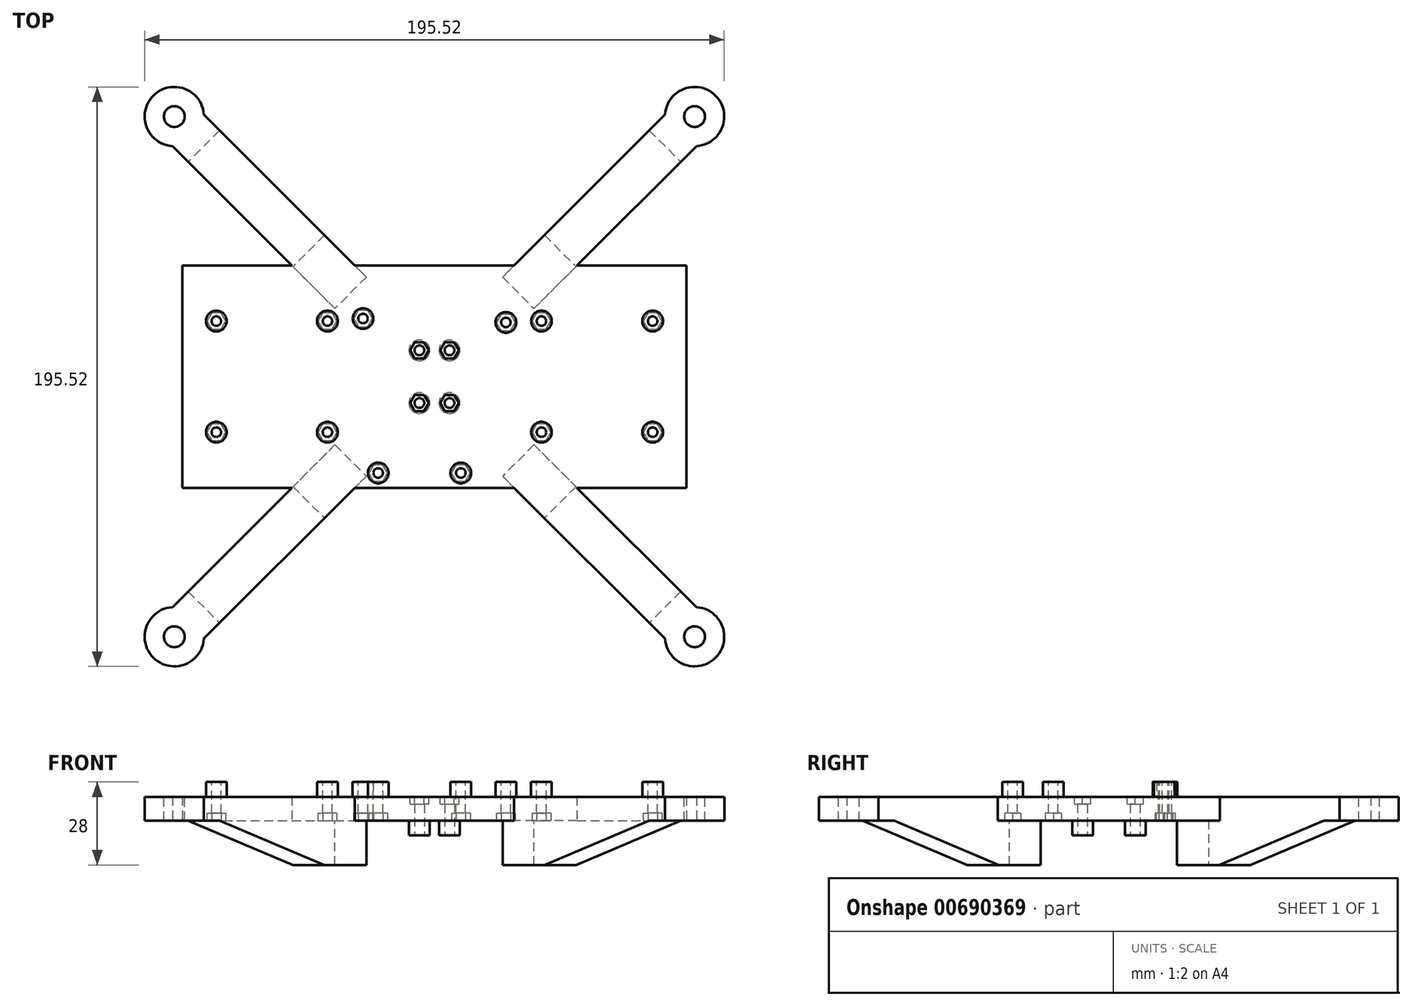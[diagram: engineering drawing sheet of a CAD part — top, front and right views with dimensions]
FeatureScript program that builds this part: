
annotation { "Feature Type Name" : "Feature", "Feature Type Description" : "" }
export const myFeature = defineFeature(function(context is Context, id is Id, definition is map)
    precondition{}
    {
        {
            var Q0;
            Q0=qCreatedBy(makeId("Top.planeOp"),FACE);
            var sketch = newSketch(context, id + "F0", { "sketchPlane" : qUnion([Q0])});
            skLineSegment(sketch, "E0.left", {"start": v(-85, 37.5) * mm, "end": v(-85, -37.5) * mm});
            skLineSegment(sketch, "E0.right", {"start": v(85, 37.5) * mm, "end": v(85, -37.5) * mm});
            skPoint(sketch, "E0.middle", {"position": v(0, 0) * mm});
            skLineSegment(sketch, "E1", {"start": v(-10.6, 0) * mm, "end": v(-48.1, 37.5) * mm, "construction": true});
            skLineSegment(sketch, "E2", {"start": v(-48.1, 37.5) * mm, "end": v(-88.39, 77.78) * mm});
            skLineSegment(sketch, "E3", {"start": v(0, 10.6) * mm, "end": v(-26.9, 37.5) * mm, "construction": true});
            skLineSegment(sketch, "E4", {"start": v(-26.9, 37.5) * mm, "end": v(-77.78, 88.39) * mm});
            skLineSegment(sketch, "E5", {"start": v(0, 10.6) * mm, "end": v(26.9, 37.5) * mm, "construction": true});
            skLineSegment(sketch, "E6", {"start": v(26.9, 37.5) * mm, "end": v(77.78, 88.39) * mm});
            skLineSegment(sketch, "E7", {"start": v(10.6, 0) * mm, "end": v(48.1, 37.5) * mm, "construction": true});
            skLineSegment(sketch, "E8", {"start": v(48.1, 37.5) * mm, "end": v(88.39, 77.78) * mm});
            skLineSegment(sketch, "E9", {"start": v(-10.6, 0) * mm, "end": v(-48.1, -37.5) * mm, "construction": true});
            skLineSegment(sketch, "E10", {"start": v(-48.1, -37.5) * mm, "end": v(-88.39, -77.78) * mm});
            skLineSegment(sketch, "E11", {"start": v(0, -10.6) * mm, "end": v(-26.9, -37.5) * mm, "construction": true});
            skLineSegment(sketch, "E12", {"start": v(-26.9, -37.5) * mm, "end": v(-77.78, -88.39) * mm});
            skLineSegment(sketch, "E13", {"start": v(0, -10.6) * mm, "end": v(26.9, -37.5) * mm, "construction": true});
            skLineSegment(sketch, "E14", {"start": v(26.9, -37.5) * mm, "end": v(77.78, -88.39) * mm});
            skLineSegment(sketch, "E15", {"start": v(10.6, 0) * mm, "end": v(48.1, -37.5) * mm, "construction": true});
            skLineSegment(sketch, "E16", {"start": v(48.1, -37.5) * mm, "end": v(88.39, -77.78) * mm});
            skLineSegment(sketch, "E17", {"start": v(0, 10.6) * mm, "end": v(0, -10.6) * mm, "construction": true});
            skLineSegment(sketch, "E18", {"start": v(-10.6, 0) * mm, "end": v(10.6, 0) * mm, "construction": true});
            skLineSegment(sketch, "E19", {"start": v(-85, 37.5) * mm, "end": v(-48.1, 37.5) * mm});
            skLineSegment(sketch, "E20", {"start": v(-26.9, 37.5) * mm, "end": v(26.9, 37.5) * mm});
            skLineSegment(sketch, "E21", {"start": v(85, 37.5) * mm, "end": v(48.1, 37.5) * mm});
            skLineSegment(sketch, "E22", {"start": v(-85, -37.5) * mm, "end": v(-48.1, -37.5) * mm});
            skLineSegment(sketch, "E23", {"start": v(-26.9, -37.5) * mm, "end": v(26.9, -37.5) * mm});
            skLineSegment(sketch, "E24", {"start": v(48.1, -37.5) * mm, "end": v(85, -37.5) * mm});
            skArc(sketch, "E25", {"start": v(-77.78, 88.39) * mm, "mid": v(-94.83, 94.83) * mm, "end": v(-88.39, 77.78) * mm});
            skArc(sketch, "E26", {"start": v(77.78, 88.39) * mm, "mid": v(94.83, 94.83) * mm, "end": v(88.39, 77.78) * mm});
            skArc(sketch, "E27", {"start": v(88.39, -77.78) * mm, "mid": v(94.83, -94.83) * mm, "end": v(77.78, -88.39) * mm});
            skArc(sketch, "E28", {"start": v(-88.39, -77.78) * mm, "mid": v(-94.83, -94.83) * mm, "end": v(-77.78, -88.39) * mm});
            skSolve(sketch);
        }
        {
            var Q0;
            Q0 = qSketchRegion(id + "F0", true);
            extrude(context, id + "F1", {"entities" : qUnion([Q0]), "endBound" : BoundingType.SYMMETRIC, "depth" : 8 * mm, "offsetDistance" : 25.4 * mm});
        }
        {
            var Q0;
            Q0=makeQuery(id+"F1.opExtrude","SWEPT_FACE",FACE,{"disambiguationData":[OSD([sQuery(id+"F0.wireOp",EDGE,"E12")])]});
            cPlane(context, id + "F2", {"entities" : qUnion([Q0]), "cplaneType" : CPlaneType.OFFSET, "offset" : 0 * mm, "width" : 152.4 * mm, "height" : 152.4 * mm});
        }
        {
            var Q0;
            Q0=qCreatedBy(id+"F2.planeOp",FACE);
            var sketch = newSketch(context, id + "F3", { "sketchPlane" : qUnion([Q0])});
            skLineSegment(sketch, "E29", {"start": v(-110, -4) * mm, "end": v(-60, -19) * mm});
            skLineSegment(sketch, "E30", {"start": v(-60, -19) * mm, "end": v(-40, -19) * mm});
            skLineSegment(sketch, "E31", {"start": v(-40, -19) * mm, "end": v(-40, -4) * mm});
            skLineSegment(sketch, "E32", {"start": v(-40, -4) * mm, "end": v(-110, -4) * mm});
            skLineSegment(sketch, "E33", {"start": v(0, 36.74) * mm, "end": v(0, -57.68) * mm, "construction": true});
            skLineSegment(sketch, "E34.MirrorCS", {"start": v(40, -19) * mm, "end": v(40, -4) * mm});
            skLineSegment(sketch, "E35.MirrorCS", {"start": v(40, -4) * mm, "end": v(110, -4) * mm});
            skLineSegment(sketch, "E36.MirrorCS", {"start": v(110, -4) * mm, "end": v(60, -19) * mm});
            skLineSegment(sketch, "E37.MirrorCS", {"start": v(60, -19) * mm, "end": v(40, -19) * mm});
            skSolve(sketch);
        }
        {
            var Q0;
            Q0 = qSketchRegion(id + "F3", true);
            var Q1;
            Q1=makeQuery(id+"F1.opExtrude","SWEPT_FACE",FACE,{"disambiguationData":[OSD([sQuery(id+"F0.wireOp",EDGE,"E10")])]});
            extrude(context, id + "F4", {"entities" : qUnion([Q0]), "operationType" : NewBodyOperationType.ADD, "endBound" : BoundingType.UP_TO_SURFACE, "oppositeDirection" : true, "depth" : 15 * mm, "endBoundEntityFace" : qUnion([Q1]), "offsetDistance" : 25.4 * mm});
        }
        {
            var Q0;
            Q0=makeQuery(id+"F1.opExtrude","SWEPT_FACE",FACE,{"disambiguationData":[OSD([sQuery(id+"F0.wireOp",EDGE,"E2")])]});
            cPlane(context, id + "F5", {"entities" : qUnion([Q0]), "cplaneType" : CPlaneType.OFFSET, "offset" : 0 * mm, "width" : 152.4 * mm, "height" : 152.4 * mm});
        }
        {
            var Q0;
            Q0=qCreatedBy(id+"F5.planeOp",FACE);
            var sketch = newSketch(context, id + "F6", { "sketchPlane" : qUnion([Q0])});
            skLineSegment(sketch, "E38", {"start": v(0, 30.92) * mm, "end": v(0, -51.6) * mm, "construction": true});
            skLineSegment(sketch, "E39", {"start": v(-40, -4) * mm, "end": v(-110, -4) * mm});
            skLineSegment(sketch, "E40", {"start": v(-110, -4) * mm, "end": v(-60, -19) * mm});
            skLineSegment(sketch, "E41", {"start": v(-60, -19) * mm, "end": v(-40, -19) * mm});
            skLineSegment(sketch, "E42", {"start": v(-40, -19) * mm, "end": v(-40, -4) * mm});
            skLineSegment(sketch, "E43.MirrorCS", {"start": v(40, -19) * mm, "end": v(40, -4) * mm});
            skLineSegment(sketch, "E44.MirrorCS", {"start": v(40, -4) * mm, "end": v(110, -4) * mm});
            skLineSegment(sketch, "E45.MirrorCS", {"start": v(110, -4) * mm, "end": v(60, -19) * mm});
            skLineSegment(sketch, "E46.MirrorCS", {"start": v(60, -19) * mm, "end": v(40, -19) * mm});
            skSolve(sketch);
        }
        {
            var Q0;
            Q0 = qSketchRegion(id + "F6", true);
            var Q1;
            Q1=makeQuery(id+"F1.opExtrude","SWEPT_FACE",FACE,{"disambiguationData":[OSD([sQuery(id+"F0.wireOp",EDGE,"E4")])]});
            extrude(context, id + "F7", {"entities" : qUnion([Q0]), "operationType" : NewBodyOperationType.ADD, "endBound" : BoundingType.UP_TO_SURFACE, "oppositeDirection" : true, "depth" : 25.4 * mm, "endBoundEntityFace" : qUnion([Q1]), "offsetDistance" : 25.4 * mm});
        }
        {
            var Q0;
            Q0=makeQuery(id+"F1.opExtrude","CAP_FACE",FACE,{"disambiguationData":[OSD([sQuery(id+"F0.wireOp",EDGE,"E0.left"),sQuery(id+"F0.wireOp",EDGE,"E0.right"),sQuery(id+"F0.wireOp",EDGE,"E2"),sQuery(id+"F0.wireOp",EDGE,"E4"),sQuery(id+"F0.wireOp",EDGE,"E6"),sQuery(id+"F0.wireOp",EDGE,"E8"),sQuery(id+"F0.wireOp",EDGE,"E10"),sQuery(id+"F0.wireOp",EDGE,"E12"),sQuery(id+"F0.wireOp",EDGE,"E14"),sQuery(id+"F0.wireOp",EDGE,"E16"),sQuery(id+"F0.wireOp",EDGE,"E19"),sQuery(id+"F0.wireOp",EDGE,"E20"),sQuery(id+"F0.wireOp",EDGE,"E21"),sQuery(id+"F0.wireOp",EDGE,"E22"),sQuery(id+"F0.wireOp",EDGE,"E23"),sQuery(id+"F0.wireOp",EDGE,"E24"),sQuery(id+"F0.wireOp",EDGE,"E25"),sQuery(id+"F0.wireOp",EDGE,"E26"),sQuery(id+"F0.wireOp",EDGE,"E27"),sQuery(id+"F0.wireOp",EDGE,"E28")])],"isStart":false});
            var sketch = newSketch(context, id + "F8", { "sketchPlane" : qUnion([Q0])});
            skCircle(sketch, "E47", {"center": v(-87.76, 87.76) * mm, "radius": 3.5 * mm});
            skCircle(sketch, "E48", {"center": v(87.76, 87.76) * mm, "radius": 3.5 * mm});
            skCircle(sketch, "E49", {"center": v(87.76, -87.76) * mm, "radius": 3.5 * mm});
            skCircle(sketch, "E50", {"center": v(-87.76, -87.76) * mm, "radius": 3.5 * mm});
            skSolve(sketch);
        }
        {
            var Q0;
            Q0 = qSketchRegion(id + "F8", true);
            extrude(context, id + "F9", {"entities" : qUnion([Q0]), "operationType" : NewBodyOperationType.REMOVE, "endBound" : BoundingType.THROUGH_ALL, "oppositeDirection" : true, "depth" : 25.4 * mm, "offsetDistance" : 25.4 * mm});
        }
        {
            var Q0;
            Q0=makeQuery(id+"F1.opExtrude","CAP_FACE",FACE,{"disambiguationData":[OSD([sQuery(id+"F0.wireOp",EDGE,"E0.left"),sQuery(id+"F0.wireOp",EDGE,"E0.right"),sQuery(id+"F0.wireOp",EDGE,"E2"),sQuery(id+"F0.wireOp",EDGE,"E4"),sQuery(id+"F0.wireOp",EDGE,"E6"),sQuery(id+"F0.wireOp",EDGE,"E8"),sQuery(id+"F0.wireOp",EDGE,"E10"),sQuery(id+"F0.wireOp",EDGE,"E12"),sQuery(id+"F0.wireOp",EDGE,"E14"),sQuery(id+"F0.wireOp",EDGE,"E16"),sQuery(id+"F0.wireOp",EDGE,"E19"),sQuery(id+"F0.wireOp",EDGE,"E20"),sQuery(id+"F0.wireOp",EDGE,"E21"),sQuery(id+"F0.wireOp",EDGE,"E22"),sQuery(id+"F0.wireOp",EDGE,"E23"),sQuery(id+"F0.wireOp",EDGE,"E24"),sQuery(id+"F0.wireOp",EDGE,"E25"),sQuery(id+"F0.wireOp",EDGE,"E26"),sQuery(id+"F0.wireOp",EDGE,"E27"),sQuery(id+"F0.wireOp",EDGE,"E28")])],"isStart":false});
            var sketch = newSketch(context, id + "F10", { "sketchPlane" : qUnion([Q0])});
            skCircle(sketch, "E51", {"center": v(-24.1, 19.6) * mm, "radius": 1.6 * mm});
            skCircle(sketch, "E52", {"center": v(24.1, 18.3) * mm, "radius": 1.6 * mm});
            skCircle(sketch, "E53", {"center": v(-19, -32.5) * mm, "radius": 1.6 * mm});
            skCircle(sketch, "E54", {"center": v(8.9, -32.5) * mm, "radius": 1.6 * mm});
            skLineSegment(sketch, "E55", {"start": v(-24.1, 19.6) * mm, "end": v(-24.1, 28.34) * mm, "construction": true});
            skLineSegment(sketch, "E56", {"start": v(-24.1, 28.34) * mm, "end": v(24.1, 28.34) * mm, "construction": true});
            skLineSegment(sketch, "E57", {"start": v(24.1, 28.34) * mm, "end": v(24.1, 18.3) * mm, "construction": true});
            skLineSegment(sketch, "E58", {"start": v(0, -37.5) * mm, "end": v(0, 37.5) * mm, "construction": true});
            skLineSegment(sketch, "E59", {"start": v(-19, -32.5) * mm, "end": v(-19, 32.5) * mm, "construction": true});
            skLineSegment(sketch, "E60", {"start": v(-85, 0) * mm, "end": v(85, 0) * mm, "construction": true});
            skCircle(sketch, "E61", {"center": v(-36.1, 18.75) * mm, "radius": 1.6 * mm});
            skCircle(sketch, "E62", {"center": v(-73.6, 18.75) * mm, "radius": 1.6 * mm});
            skCircle(sketch, "E63", {"center": v(-73.6, -18.75) * mm, "radius": 1.6 * mm});
            skCircle(sketch, "E64", {"center": v(-36.1, -18.75) * mm, "radius": 1.6 * mm});
            skLineSegment(sketch, "E65", {"start": v(-73.6, 18.75) * mm, "end": v(-36.1, 18.75) * mm, "construction": true});
            skLineSegment(sketch, "E66", {"start": v(-36.1, -18.75) * mm, "end": v(-36.1, 18.75) * mm, "construction": true});
            skLineSegment(sketch, "E67", {"start": v(-73.6, 18.75) * mm, "end": v(-73.6, -18.75) * mm, "construction": true});
            skLineSegment(sketch, "E68", {"start": v(-73.6, -18.75) * mm, "end": v(-36.1, -18.75) * mm, "construction": true});
            skCircle(sketch, "E69.MirrorC", {"center": v(36.1, 18.75) * mm, "radius": 1.6 * mm});
            skCircle(sketch, "E70.MirrorC", {"center": v(36.1, -18.75) * mm, "radius": 1.6 * mm});
            skCircle(sketch, "E71.MirrorC", {"center": v(73.6, -18.75) * mm, "radius": 1.6 * mm});
            skCircle(sketch, "E72.MirrorC", {"center": v(73.6, 18.75) * mm, "radius": 1.6 * mm});
            skSolve(sketch);
        }
        {
            var Q0;
            Q0 = qSketchRegion(id + "F10", true);
            extrude(context, id + "F11", {"entities" : qUnion([Q0]), "operationType" : NewBodyOperationType.REMOVE, "endBound" : BoundingType.THROUGH_ALL, "oppositeDirection" : true, "depth" : 25.4 * mm, "offsetDistance" : 25.4 * mm});
        }
        {
            var Q0;
            {var subQ0=sQuery(id+"F0.wireOp",EDGE,"E10");var subQ2=sQuery(id+"F0.wireOp",EDGE,"E24");var subQ6=sQuery(id+"F0.wireOp",EDGE,"E19");var subQ9=sQuery(id+"F0.wireOp",EDGE,"E16");var subQ13=sQuery(id+"F0.wireOp",EDGE,"E12");var subQ15=sQuery(id+"F0.wireOp",EDGE,"E23");var subQ18=sQuery(id+"F0.wireOp",EDGE,"E22");var subQ21=sQuery(id+"F0.wireOp",EDGE,"E8");var subQ23=sQuery(id+"F0.wireOp",EDGE,"E21");var subQ25=sQuery(id+"F0.wireOp",EDGE,"E20");var subQ27=sQuery(id+"F0.wireOp",EDGE,"E2");var subQ29=sQuery(id+"F0.wireOp",EDGE,"E0.right");var subQ31=sQuery(id+"F0.wireOp",EDGE,"E4");var subQ33=sQuery(id+"F0.wireOp",EDGE,"E0.left");var subQ34=makeQuery(id+"F1.opExtrude","SWEPT_FACE",FACE,{"disambiguationData":[OSD([subQ33])]});var subQ35=sQuery(id+"F0.wireOp",EDGE,"E6");var subQ38=sQuery(id+"F0.wireOp",EDGE,"E14");var subQ42=sQuery(id+"F0.wireOp",EDGE,"E27");var subQ43=sQuery(id+"F0.wireOp",EDGE,"E25");Q0=makeQuery(id+"F7.boolean.opBoolean","SPLIT",FACE,{"disambiguationData":[TD([subQ34])],"derivedFrom":makeQuery(id+"F4.boolean.opBoolean","SPLIT",FACE,{"disambiguationData":[TD([subQ34])],"derivedFrom":makeQuery(id+"F1.opExtrude","CAP_FACE",FACE,{"disambiguationData":[OSD([subQ33,subQ29,subQ27,subQ31,subQ35,subQ21,subQ0,subQ13,subQ38,subQ9,subQ6,subQ25,subQ23,subQ18,subQ15,subQ2,subQ43,sQuery(id+"F0.wireOp",EDGE,"E26"),subQ42,sQuery(id+"F0.wireOp",EDGE,"E28")])],"isStart":true})})});}
            var sketch = newSketch(context, id + "F12", { "sketchPlane" : qUnion([Q0])});
            skCircle(sketch, "E73.cCircle", {"center": v(-19, 32.5) * mm, "radius": 2.75 * mm, "construction": true});
            skLineSegment(sketch, "E73.0", {"start": v(-22.18, 32.5) * mm, "end": v(-20.59, 35.25) * mm});
            skLineSegment(sketch, "E73.1", {"start": v(-20.59, 35.25) * mm, "end": v(-17.41, 35.25) * mm});
            skLineSegment(sketch, "E73.2", {"start": v(-17.41, 35.25) * mm, "end": v(-15.82, 32.5) * mm});
            skLineSegment(sketch, "E73.3", {"start": v(-15.82, 32.5) * mm, "end": v(-17.41, 29.75) * mm});
            skLineSegment(sketch, "E73.4", {"start": v(-17.41, 29.75) * mm, "end": v(-20.59, 29.75) * mm});
            skLineSegment(sketch, "E73.5", {"start": v(-20.59, 29.75) * mm, "end": v(-22.18, 32.5) * mm});
            skPoint(sketch, "E73.0.midPoint", {"position": v(-21.38, 33.87) * mm});
            skCircle(sketch, "E74.cCircle", {"center": v(8.9, 32.5) * mm, "radius": 2.75 * mm, "construction": true});
            skLineSegment(sketch, "E74.0", {"start": v(5.72, 32.5) * mm, "end": v(7.31, 35.25) * mm});
            skLineSegment(sketch, "E74.1", {"start": v(7.31, 35.25) * mm, "end": v(10.49, 35.25) * mm});
            skLineSegment(sketch, "E74.2", {"start": v(10.49, 35.25) * mm, "end": v(12.08, 32.5) * mm});
            skLineSegment(sketch, "E74.3", {"start": v(12.08, 32.5) * mm, "end": v(10.49, 29.75) * mm});
            skLineSegment(sketch, "E74.4", {"start": v(10.49, 29.75) * mm, "end": v(7.31, 29.75) * mm});
            skLineSegment(sketch, "E74.5", {"start": v(7.31, 29.75) * mm, "end": v(5.72, 32.5) * mm});
            skPoint(sketch, "E74.0.midPoint", {"position": v(6.52, 33.88) * mm});
            skCircle(sketch, "E75.cCircle", {"center": v(36.1, 18.75) * mm, "radius": 2.75 * mm, "construction": true});
            skLineSegment(sketch, "E75.0", {"start": v(32.92, 18.75) * mm, "end": v(34.51, 21.5) * mm});
            skLineSegment(sketch, "E75.1", {"start": v(34.51, 21.5) * mm, "end": v(37.69, 21.5) * mm});
            skLineSegment(sketch, "E75.2", {"start": v(37.69, 21.5) * mm, "end": v(39.28, 18.75) * mm});
            skLineSegment(sketch, "E75.3", {"start": v(39.28, 18.75) * mm, "end": v(37.69, 16) * mm});
            skLineSegment(sketch, "E75.4", {"start": v(37.69, 16) * mm, "end": v(34.51, 16) * mm});
            skLineSegment(sketch, "E75.5", {"start": v(34.51, 16) * mm, "end": v(32.92, 18.75) * mm});
            skPoint(sketch, "E75.0.midPoint", {"position": v(33.72, 20.12) * mm});
            skCircle(sketch, "E76.cCircle", {"center": v(73.6, 18.75) * mm, "radius": 2.75 * mm, "construction": true});
            skLineSegment(sketch, "E76.0", {"start": v(70.42, 18.75) * mm, "end": v(72.01, 21.5) * mm});
            skLineSegment(sketch, "E76.1", {"start": v(72.01, 21.5) * mm, "end": v(75.19, 21.5) * mm});
            skLineSegment(sketch, "E76.2", {"start": v(75.19, 21.5) * mm, "end": v(76.78, 18.75) * mm});
            skLineSegment(sketch, "E76.3", {"start": v(76.78, 18.75) * mm, "end": v(75.19, 16) * mm});
            skLineSegment(sketch, "E76.4", {"start": v(75.19, 16) * mm, "end": v(72.01, 16) * mm});
            skLineSegment(sketch, "E76.5", {"start": v(72.01, 16) * mm, "end": v(70.42, 18.75) * mm});
            skPoint(sketch, "E76.0.midPoint", {"position": v(71.22, 20.12) * mm});
            skCircle(sketch, "E77.cCircle", {"center": v(73.6, -18.75) * mm, "radius": 2.75 * mm, "construction": true});
            skLineSegment(sketch, "E77.0", {"start": v(70.42, -18.75) * mm, "end": v(72.01, -16) * mm});
            skLineSegment(sketch, "E77.1", {"start": v(72.01, -16) * mm, "end": v(75.19, -16) * mm});
            skLineSegment(sketch, "E77.2", {"start": v(75.19, -16) * mm, "end": v(76.78, -18.75) * mm});
            skLineSegment(sketch, "E77.3", {"start": v(76.78, -18.75) * mm, "end": v(75.19, -21.5) * mm});
            skLineSegment(sketch, "E77.4", {"start": v(75.19, -21.5) * mm, "end": v(72.01, -21.5) * mm});
            skLineSegment(sketch, "E77.5", {"start": v(72.01, -21.5) * mm, "end": v(70.42, -18.75) * mm});
            skPoint(sketch, "E77.0.midPoint", {"position": v(71.22, -17.37) * mm});
            skCircle(sketch, "E78.cCircle", {"center": v(36.1, -18.75) * mm, "radius": 2.75 * mm, "construction": true});
            skLineSegment(sketch, "E78.0", {"start": v(34.51, -16) * mm, "end": v(37.69, -16) * mm});
            skLineSegment(sketch, "E78.1", {"start": v(37.69, -16) * mm, "end": v(39.28, -18.75) * mm});
            skLineSegment(sketch, "E78.2", {"start": v(39.28, -18.75) * mm, "end": v(37.69, -21.5) * mm});
            skLineSegment(sketch, "E78.3", {"start": v(37.69, -21.5) * mm, "end": v(34.51, -21.5) * mm});
            skLineSegment(sketch, "E78.4", {"start": v(34.51, -21.5) * mm, "end": v(32.92, -18.75) * mm});
            skLineSegment(sketch, "E78.5", {"start": v(32.92, -18.75) * mm, "end": v(34.51, -16) * mm});
            skPoint(sketch, "E78.0.midPoint", {"position": v(36.1, -16) * mm});
            skCircle(sketch, "E79.cCircle", {"center": v(24.1, -18.3) * mm, "radius": 2.75 * mm, "construction": true});
            skLineSegment(sketch, "E79.0", {"start": v(20.92, -18.3) * mm, "end": v(22.51, -15.55) * mm});
            skLineSegment(sketch, "E79.1", {"start": v(22.51, -15.55) * mm, "end": v(25.69, -15.55) * mm});
            skLineSegment(sketch, "E79.2", {"start": v(25.69, -15.55) * mm, "end": v(27.28, -18.3) * mm});
            skLineSegment(sketch, "E79.3", {"start": v(27.28, -18.3) * mm, "end": v(25.69, -21.05) * mm});
            skLineSegment(sketch, "E79.4", {"start": v(25.69, -21.05) * mm, "end": v(22.51, -21.05) * mm});
            skLineSegment(sketch, "E79.5", {"start": v(22.51, -21.05) * mm, "end": v(20.92, -18.3) * mm});
            skPoint(sketch, "E79.0.midPoint", {"position": v(21.72, -16.93) * mm});
            skCircle(sketch, "E80.cCircle", {"center": v(-24.1, -19.6) * mm, "radius": 2.75 * mm, "construction": true});
            skLineSegment(sketch, "E80.0", {"start": v(-25.69, -16.85) * mm, "end": v(-22.51, -16.85) * mm});
            skLineSegment(sketch, "E80.1", {"start": v(-22.51, -16.85) * mm, "end": v(-20.92, -19.6) * mm});
            skLineSegment(sketch, "E80.2", {"start": v(-20.92, -19.6) * mm, "end": v(-22.51, -22.35) * mm});
            skLineSegment(sketch, "E80.3", {"start": v(-22.51, -22.35) * mm, "end": v(-25.69, -22.35) * mm});
            skLineSegment(sketch, "E80.4", {"start": v(-25.69, -22.35) * mm, "end": v(-27.28, -19.6) * mm});
            skLineSegment(sketch, "E80.5", {"start": v(-27.28, -19.6) * mm, "end": v(-25.69, -16.85) * mm});
            skPoint(sketch, "E80.0.midPoint", {"position": v(-24.1, -16.85) * mm});
            skCircle(sketch, "E81.cCircle", {"center": v(-36.1, -18.75) * mm, "radius": 2.75 * mm, "construction": true});
            skLineSegment(sketch, "E81.0", {"start": v(-37.69, -16) * mm, "end": v(-34.51, -16) * mm});
            skLineSegment(sketch, "E81.1", {"start": v(-34.51, -16) * mm, "end": v(-32.92, -18.75) * mm});
            skLineSegment(sketch, "E81.2", {"start": v(-32.92, -18.75) * mm, "end": v(-34.51, -21.5) * mm});
            skLineSegment(sketch, "E81.3", {"start": v(-34.51, -21.5) * mm, "end": v(-37.69, -21.5) * mm});
            skLineSegment(sketch, "E81.4", {"start": v(-37.69, -21.5) * mm, "end": v(-39.28, -18.75) * mm});
            skLineSegment(sketch, "E81.5", {"start": v(-39.28, -18.75) * mm, "end": v(-37.69, -16) * mm});
            skPoint(sketch, "E81.0.midPoint", {"position": v(-36.1, -16) * mm});
            skCircle(sketch, "E82.cCircle", {"center": v(-36.1, 18.75) * mm, "radius": 2.75 * mm, "construction": true});
            skLineSegment(sketch, "E82.0", {"start": v(-39.28, 18.75) * mm, "end": v(-37.69, 21.5) * mm});
            skLineSegment(sketch, "E82.1", {"start": v(-37.69, 21.5) * mm, "end": v(-34.51, 21.5) * mm});
            skLineSegment(sketch, "E82.2", {"start": v(-34.51, 21.5) * mm, "end": v(-32.92, 18.75) * mm});
            skLineSegment(sketch, "E82.3", {"start": v(-32.92, 18.75) * mm, "end": v(-34.51, 16) * mm});
            skLineSegment(sketch, "E82.4", {"start": v(-34.51, 16) * mm, "end": v(-37.69, 16) * mm});
            skLineSegment(sketch, "E82.5", {"start": v(-37.69, 16) * mm, "end": v(-39.28, 18.75) * mm});
            skPoint(sketch, "E82.0.midPoint", {"position": v(-38.48, 20.12) * mm});
            skCircle(sketch, "E83.cCircle", {"center": v(-73.6, 18.75) * mm, "radius": 2.75 * mm, "construction": true});
            skLineSegment(sketch, "E83.0", {"start": v(-72.01, 21.5) * mm, "end": v(-70.42, 18.75) * mm});
            skLineSegment(sketch, "E83.1", {"start": v(-70.42, 18.75) * mm, "end": v(-72.01, 16) * mm});
            skLineSegment(sketch, "E83.2", {"start": v(-72.01, 16) * mm, "end": v(-75.19, 16) * mm});
            skLineSegment(sketch, "E83.3", {"start": v(-75.19, 16) * mm, "end": v(-76.78, 18.75) * mm});
            skLineSegment(sketch, "E83.4", {"start": v(-76.78, 18.75) * mm, "end": v(-75.19, 21.5) * mm});
            skLineSegment(sketch, "E83.5", {"start": v(-75.19, 21.5) * mm, "end": v(-72.01, 21.5) * mm});
            skPoint(sketch, "E83.0.midPoint", {"position": v(-71.22, 20.12) * mm});
            skCircle(sketch, "E84.cCircle", {"center": v(-73.6, -18.75) * mm, "radius": 2.75 * mm, "construction": true});
            skLineSegment(sketch, "E84.0", {"start": v(-72.01, -16) * mm, "end": v(-70.42, -18.75) * mm});
            skLineSegment(sketch, "E84.1", {"start": v(-70.42, -18.75) * mm, "end": v(-72.01, -21.5) * mm});
            skLineSegment(sketch, "E84.2", {"start": v(-72.01, -21.5) * mm, "end": v(-75.19, -21.5) * mm});
            skLineSegment(sketch, "E84.3", {"start": v(-75.19, -21.5) * mm, "end": v(-76.78, -18.75) * mm});
            skLineSegment(sketch, "E84.4", {"start": v(-76.78, -18.75) * mm, "end": v(-75.19, -16) * mm});
            skLineSegment(sketch, "E84.5", {"start": v(-75.19, -16) * mm, "end": v(-72.01, -16) * mm});
            skPoint(sketch, "E84.0.midPoint", {"position": v(-71.22, -17.37) * mm});
            skSolve(sketch);
        }
        {
            var Q0;
            Q0 = qSketchRegion(id + "F12", true);
            extrude(context, id + "F13", {"entities" : qUnion([Q0]), "operationType" : NewBodyOperationType.REMOVE, "oppositeDirection" : true, "depth" : 2.5 * mm, "offsetDistance" : 25.4 * mm});
        }
        {
            var Q0;
            Q0=makeQuery(id+"F1.opExtrude","CAP_FACE",FACE,{"disambiguationData":[OSD([sQuery(id+"F0.wireOp",EDGE,"E0.left"),sQuery(id+"F0.wireOp",EDGE,"E0.right"),sQuery(id+"F0.wireOp",EDGE,"E2"),sQuery(id+"F0.wireOp",EDGE,"E4"),sQuery(id+"F0.wireOp",EDGE,"E6"),sQuery(id+"F0.wireOp",EDGE,"E8"),sQuery(id+"F0.wireOp",EDGE,"E10"),sQuery(id+"F0.wireOp",EDGE,"E12"),sQuery(id+"F0.wireOp",EDGE,"E14"),sQuery(id+"F0.wireOp",EDGE,"E16"),sQuery(id+"F0.wireOp",EDGE,"E19"),sQuery(id+"F0.wireOp",EDGE,"E20"),sQuery(id+"F0.wireOp",EDGE,"E21"),sQuery(id+"F0.wireOp",EDGE,"E22"),sQuery(id+"F0.wireOp",EDGE,"E23"),sQuery(id+"F0.wireOp",EDGE,"E24"),sQuery(id+"F0.wireOp",EDGE,"E25"),sQuery(id+"F0.wireOp",EDGE,"E26"),sQuery(id+"F0.wireOp",EDGE,"E27"),sQuery(id+"F0.wireOp",EDGE,"E28")])],"isStart":false});
            var sketch = newSketch(context, id + "F14", { "sketchPlane" : qUnion([Q0])});
            skCircle(sketch, "E85", {"center": v(-24.1, 19.6) * mm, "radius": 1.6 * mm});
            skCircle(sketch, "E86", {"center": v(-19, -32.5) * mm, "radius": 1.6 * mm});
            skCircle(sketch, "E87", {"center": v(-19, -32.5) * mm, "radius": 3.5 * mm});
            skCircle(sketch, "E88", {"center": v(-24.1, 19.6) * mm, "radius": 3.5 * mm});
            skCircle(sketch, "E89", {"center": v(-36.1, 18.75) * mm, "radius": 1.6 * mm});
            skCircle(sketch, "E90", {"center": v(-36.1, 18.75) * mm, "radius": 3.5 * mm});
            skCircle(sketch, "E91", {"center": v(-73.6, 18.75) * mm, "radius": 1.6 * mm});
            skCircle(sketch, "E92", {"center": v(-73.6, 18.75) * mm, "radius": 3.5 * mm});
            skCircle(sketch, "E93", {"center": v(-73.6, -18.75) * mm, "radius": 1.6 * mm});
            skCircle(sketch, "E94", {"center": v(-73.6, -18.75) * mm, "radius": 3.5 * mm});
            skCircle(sketch, "E95", {"center": v(-36.1, -18.75) * mm, "radius": 1.6 * mm});
            skCircle(sketch, "E96", {"center": v(-36.1, -18.75) * mm, "radius": 3.5 * mm});
            skCircle(sketch, "E97", {"center": v(8.9, -32.5) * mm, "radius": 1.6 * mm});
            skCircle(sketch, "E98", {"center": v(8.9, -32.5) * mm, "radius": 3.5 * mm});
            skCircle(sketch, "E99", {"center": v(24.1, 18.3) * mm, "radius": 1.6 * mm});
            skCircle(sketch, "E100", {"center": v(24.1, 18.3) * mm, "radius": 3.5 * mm});
            skCircle(sketch, "E101", {"center": v(36.1, 18.75) * mm, "radius": 1.6 * mm});
            skCircle(sketch, "E102", {"center": v(36.1, 18.75) * mm, "radius": 3.5 * mm});
            skCircle(sketch, "E103", {"center": v(73.6, 18.75) * mm, "radius": 1.6 * mm});
            skCircle(sketch, "E104", {"center": v(73.6, 18.75) * mm, "radius": 3.5 * mm});
            skCircle(sketch, "E105", {"center": v(73.6, -18.75) * mm, "radius": 1.6 * mm});
            skCircle(sketch, "E106", {"center": v(73.6, -18.75) * mm, "radius": 3.5 * mm});
            skCircle(sketch, "E107", {"center": v(36.1, -18.75) * mm, "radius": 1.6 * mm});
            skCircle(sketch, "E108", {"center": v(36.1, -18.75) * mm, "radius": 3.5 * mm});
            skSolve(sketch);
        }
        {
            var Q0;
            Q0 = qSketchRegion(id + "F14", true);
            extrude(context, id + "F15", {"entities" : qUnion([Q0]), "operationType" : NewBodyOperationType.ADD, "depth" : 5 * mm, "offsetDistance" : 25.4 * mm});
        }
        {
            var Q0;
            {var subQ0=sQuery(id+"F0.wireOp",EDGE,"E10");var subQ2=sQuery(id+"F0.wireOp",EDGE,"E24");var subQ6=sQuery(id+"F0.wireOp",EDGE,"E19");var subQ9=sQuery(id+"F0.wireOp",EDGE,"E16");var subQ13=sQuery(id+"F0.wireOp",EDGE,"E12");var subQ15=sQuery(id+"F0.wireOp",EDGE,"E23");var subQ18=sQuery(id+"F0.wireOp",EDGE,"E22");var subQ21=sQuery(id+"F0.wireOp",EDGE,"E8");var subQ23=sQuery(id+"F0.wireOp",EDGE,"E21");var subQ25=sQuery(id+"F0.wireOp",EDGE,"E20");var subQ27=sQuery(id+"F0.wireOp",EDGE,"E2");var subQ29=sQuery(id+"F0.wireOp",EDGE,"E0.right");var subQ31=sQuery(id+"F0.wireOp",EDGE,"E4");var subQ33=sQuery(id+"F0.wireOp",EDGE,"E0.left");var subQ34=makeQuery(id+"F1.opExtrude","SWEPT_FACE",FACE,{"disambiguationData":[OSD([subQ33])]});var subQ35=sQuery(id+"F0.wireOp",EDGE,"E6");var subQ38=sQuery(id+"F0.wireOp",EDGE,"E14");var subQ42=sQuery(id+"F0.wireOp",EDGE,"E27");var subQ43=sQuery(id+"F0.wireOp",EDGE,"E25");Q0=makeQuery(id+"F7.boolean.opBoolean","SPLIT",FACE,{"disambiguationData":[TD([subQ34])],"derivedFrom":makeQuery(id+"F4.boolean.opBoolean","SPLIT",FACE,{"disambiguationData":[TD([subQ34])],"derivedFrom":makeQuery(id+"F1.opExtrude","CAP_FACE",FACE,{"disambiguationData":[OSD([subQ33,subQ29,subQ27,subQ31,subQ35,subQ21,subQ0,subQ13,subQ38,subQ9,subQ6,subQ25,subQ23,subQ18,subQ15,subQ2,subQ43,sQuery(id+"F0.wireOp",EDGE,"E26"),subQ42,sQuery(id+"F0.wireOp",EDGE,"E28")])],"isStart":true})})});}
            var sketch = newSketch(context, id + "F16", { "sketchPlane" : qUnion([Q0])});
            skCircle(sketch, "E109", {"center": v(-5.08, 8.9) * mm, "radius": 1.65 * mm});
            skCircle(sketch, "E110", {"center": v(5.08, 8.9) * mm, "radius": 1.65 * mm});
            skCircle(sketch, "E111", {"center": v(5.08, -8.9) * mm, "radius": 1.65 * mm});
            skCircle(sketch, "E112", {"center": v(-5.08, -8.9) * mm, "radius": 1.65 * mm});
            skLineSegment(sketch, "E113", {"start": v(0, 18.31) * mm, "end": v(0, -16.96) * mm, "construction": true});
            skLineSegment(sketch, "E114", {"start": v(-14.97, 0) * mm, "end": v(18.85, 0) * mm, "construction": true});
            skSolve(sketch);
        }
        {
            var Q0;
            Q0 = qSketchRegion(id + "F16", true);
            extrude(context, id + "F17", {"entities" : qUnion([Q0]), "operationType" : NewBodyOperationType.REMOVE, "endBound" : BoundingType.THROUGH_ALL, "oppositeDirection" : true, "depth" : 25.4 * mm, "offsetDistance" : 25.4 * mm});
        }
        {
            var Q0;
            Q0=makeQuery(id+"F1.opExtrude","CAP_FACE",FACE,{"disambiguationData":[OSD([sQuery(id+"F0.wireOp",EDGE,"E0.left"),sQuery(id+"F0.wireOp",EDGE,"E0.right"),sQuery(id+"F0.wireOp",EDGE,"E2"),sQuery(id+"F0.wireOp",EDGE,"E4"),sQuery(id+"F0.wireOp",EDGE,"E6"),sQuery(id+"F0.wireOp",EDGE,"E8"),sQuery(id+"F0.wireOp",EDGE,"E10"),sQuery(id+"F0.wireOp",EDGE,"E12"),sQuery(id+"F0.wireOp",EDGE,"E14"),sQuery(id+"F0.wireOp",EDGE,"E16"),sQuery(id+"F0.wireOp",EDGE,"E19"),sQuery(id+"F0.wireOp",EDGE,"E20"),sQuery(id+"F0.wireOp",EDGE,"E21"),sQuery(id+"F0.wireOp",EDGE,"E22"),sQuery(id+"F0.wireOp",EDGE,"E23"),sQuery(id+"F0.wireOp",EDGE,"E24"),sQuery(id+"F0.wireOp",EDGE,"E25"),sQuery(id+"F0.wireOp",EDGE,"E26"),sQuery(id+"F0.wireOp",EDGE,"E27"),sQuery(id+"F0.wireOp",EDGE,"E28")])],"isStart":false});
            var sketch = newSketch(context, id + "F18", { "sketchPlane" : qUnion([Q0])});
            skCircle(sketch, "E115.cCircle", {"center": v(-5.08, 8.9) * mm, "radius": 2.75 * mm, "construction": true});
            skLineSegment(sketch, "E115.0", {"start": v(-6.67, 11.64) * mm, "end": v(-3.5, 11.64) * mm});
            skLineSegment(sketch, "E115.1", {"start": v(-3.5, 11.64) * mm, "end": v(-1.9, 8.9) * mm});
            skLineSegment(sketch, "E115.2", {"start": v(-1.9, 8.9) * mm, "end": v(-3.5, 6.14) * mm});
            skLineSegment(sketch, "E115.3", {"start": v(-3.5, 6.14) * mm, "end": v(-6.67, 6.14) * mm});
            skLineSegment(sketch, "E115.4", {"start": v(-6.67, 6.14) * mm, "end": v(-8.26, 8.9) * mm});
            skLineSegment(sketch, "E115.5", {"start": v(-8.26, 8.9) * mm, "end": v(-6.67, 11.64) * mm});
            skPoint(sketch, "E115.0.midPoint", {"position": v(-5.08, 11.64) * mm});
            skCircle(sketch, "E116.cCircle", {"center": v(5.08, 8.9) * mm, "radius": 2.75 * mm, "construction": true});
            skLineSegment(sketch, "E116.0", {"start": v(6.67, 11.64) * mm, "end": v(8.26, 8.89) * mm});
            skLineSegment(sketch, "E116.1", {"start": v(8.26, 8.89) * mm, "end": v(6.67, 6.14) * mm});
            skLineSegment(sketch, "E116.2", {"start": v(6.67, 6.14) * mm, "end": v(3.5, 6.14) * mm});
            skLineSegment(sketch, "E116.3", {"start": v(3.5, 6.14) * mm, "end": v(1.9, 8.89) * mm});
            skLineSegment(sketch, "E116.4", {"start": v(1.9, 8.9) * mm, "end": v(3.5, 11.64) * mm});
            skLineSegment(sketch, "E116.5", {"start": v(3.5, 11.64) * mm, "end": v(6.67, 11.64) * mm});
            skPoint(sketch, "E116.0.midPoint", {"position": v(7.46, 10.27) * mm});
            skCircle(sketch, "E117.cCircle", {"center": v(5.08, -8.9) * mm, "radius": 2.75 * mm, "construction": true});
            skLineSegment(sketch, "E117.0", {"start": v(6.67, -6.14) * mm, "end": v(8.26, -8.9) * mm});
            skLineSegment(sketch, "E117.1", {"start": v(8.26, -8.9) * mm, "end": v(6.67, -11.64) * mm});
            skLineSegment(sketch, "E117.2", {"start": v(6.67, -11.64) * mm, "end": v(3.5, -11.64) * mm});
            skLineSegment(sketch, "E117.3", {"start": v(3.5, -11.64) * mm, "end": v(1.9, -8.9) * mm});
            skLineSegment(sketch, "E117.4", {"start": v(1.9, -8.9) * mm, "end": v(3.5, -6.14) * mm});
            skLineSegment(sketch, "E117.5", {"start": v(3.5, -6.14) * mm, "end": v(6.67, -6.14) * mm});
            skPoint(sketch, "E117.0.midPoint", {"position": v(7.46, -7.52) * mm});
            skCircle(sketch, "E118.cCircle", {"center": v(-5.08, -8.9) * mm, "radius": 2.75 * mm, "construction": true});
            skLineSegment(sketch, "E118.0", {"start": v(-6.67, -6.14) * mm, "end": v(-3.5, -6.14) * mm});
            skLineSegment(sketch, "E118.1", {"start": v(-3.5, -6.14) * mm, "end": v(-1.9, -8.9) * mm});
            skLineSegment(sketch, "E118.2", {"start": v(-1.9, -8.9) * mm, "end": v(-3.5, -11.64) * mm});
            skLineSegment(sketch, "E118.3", {"start": v(-3.5, -11.64) * mm, "end": v(-6.67, -11.64) * mm});
            skLineSegment(sketch, "E118.4", {"start": v(-6.67, -11.64) * mm, "end": v(-8.26, -8.9) * mm});
            skLineSegment(sketch, "E118.5", {"start": v(-8.26, -8.9) * mm, "end": v(-6.67, -6.14) * mm});
            skPoint(sketch, "E118.0.midPoint", {"position": v(-5.08, -6.14) * mm});
            skSolve(sketch);
        }
        {
            var Q0;
            Q0 = qSketchRegion(id + "F18", true);
            extrude(context, id + "F19", {"entities" : qUnion([Q0]), "operationType" : NewBodyOperationType.REMOVE, "oppositeDirection" : true, "depth" : 2.5 * mm, "offsetDistance" : 25.4 * mm});
        }
        {
            var Q0;
            {var subQ0=sQuery(id+"F0.wireOp",EDGE,"E10");var subQ2=sQuery(id+"F0.wireOp",EDGE,"E24");var subQ6=sQuery(id+"F0.wireOp",EDGE,"E19");var subQ9=sQuery(id+"F0.wireOp",EDGE,"E16");var subQ13=sQuery(id+"F0.wireOp",EDGE,"E12");var subQ15=sQuery(id+"F0.wireOp",EDGE,"E23");var subQ18=sQuery(id+"F0.wireOp",EDGE,"E22");var subQ21=sQuery(id+"F0.wireOp",EDGE,"E8");var subQ23=sQuery(id+"F0.wireOp",EDGE,"E21");var subQ25=sQuery(id+"F0.wireOp",EDGE,"E20");var subQ27=sQuery(id+"F0.wireOp",EDGE,"E2");var subQ29=sQuery(id+"F0.wireOp",EDGE,"E0.right");var subQ31=sQuery(id+"F0.wireOp",EDGE,"E4");var subQ33=sQuery(id+"F0.wireOp",EDGE,"E0.left");var subQ34=makeQuery(id+"F1.opExtrude","SWEPT_FACE",FACE,{"disambiguationData":[OSD([subQ33])]});var subQ35=sQuery(id+"F0.wireOp",EDGE,"E6");var subQ38=sQuery(id+"F0.wireOp",EDGE,"E14");var subQ42=sQuery(id+"F0.wireOp",EDGE,"E27");var subQ43=sQuery(id+"F0.wireOp",EDGE,"E25");Q0=makeQuery(id+"F7.boolean.opBoolean","SPLIT",FACE,{"disambiguationData":[TD([subQ34])],"derivedFrom":makeQuery(id+"F4.boolean.opBoolean","SPLIT",FACE,{"disambiguationData":[TD([subQ34])],"derivedFrom":makeQuery(id+"F1.opExtrude","CAP_FACE",FACE,{"disambiguationData":[OSD([subQ33,subQ29,subQ27,subQ31,subQ35,subQ21,subQ0,subQ13,subQ38,subQ9,subQ6,subQ25,subQ23,subQ18,subQ15,subQ2,subQ43,sQuery(id+"F0.wireOp",EDGE,"E26"),subQ42,sQuery(id+"F0.wireOp",EDGE,"E28")])],"isStart":true})})});}
            var sketch = newSketch(context, id + "F20", { "sketchPlane" : qUnion([Q0])});
            skCircle(sketch, "E119", {"center": v(-5.08, -8.9) * mm, "radius": 1.65 * mm});
            skCircle(sketch, "E120", {"center": v(-5.08, -8.9) * mm, "radius": 3.5 * mm});
            skCircle(sketch, "E121", {"center": v(-5.08, 8.9) * mm, "radius": 1.65 * mm});
            skCircle(sketch, "E122", {"center": v(-5.08, 8.9) * mm, "radius": 3.5 * mm});
            skCircle(sketch, "E123", {"center": v(5.08, 8.9) * mm, "radius": 1.65 * mm});
            skCircle(sketch, "E124", {"center": v(5.08, 8.9) * mm, "radius": 3.5 * mm});
            skCircle(sketch, "E125", {"center": v(5.08, -8.9) * mm, "radius": 1.65 * mm});
            skCircle(sketch, "E126", {"center": v(5.08, -8.9) * mm, "radius": 3.5 * mm});
            skSolve(sketch);
        }
        {
            var Q0;
            Q0 = qSketchRegion(id + "F20", true);
            extrude(context, id + "F21", {"entities" : qUnion([Q0]), "operationType" : NewBodyOperationType.ADD, "depth" : 5 * mm, "offsetDistance" : 25.4 * mm});
        }
    });
